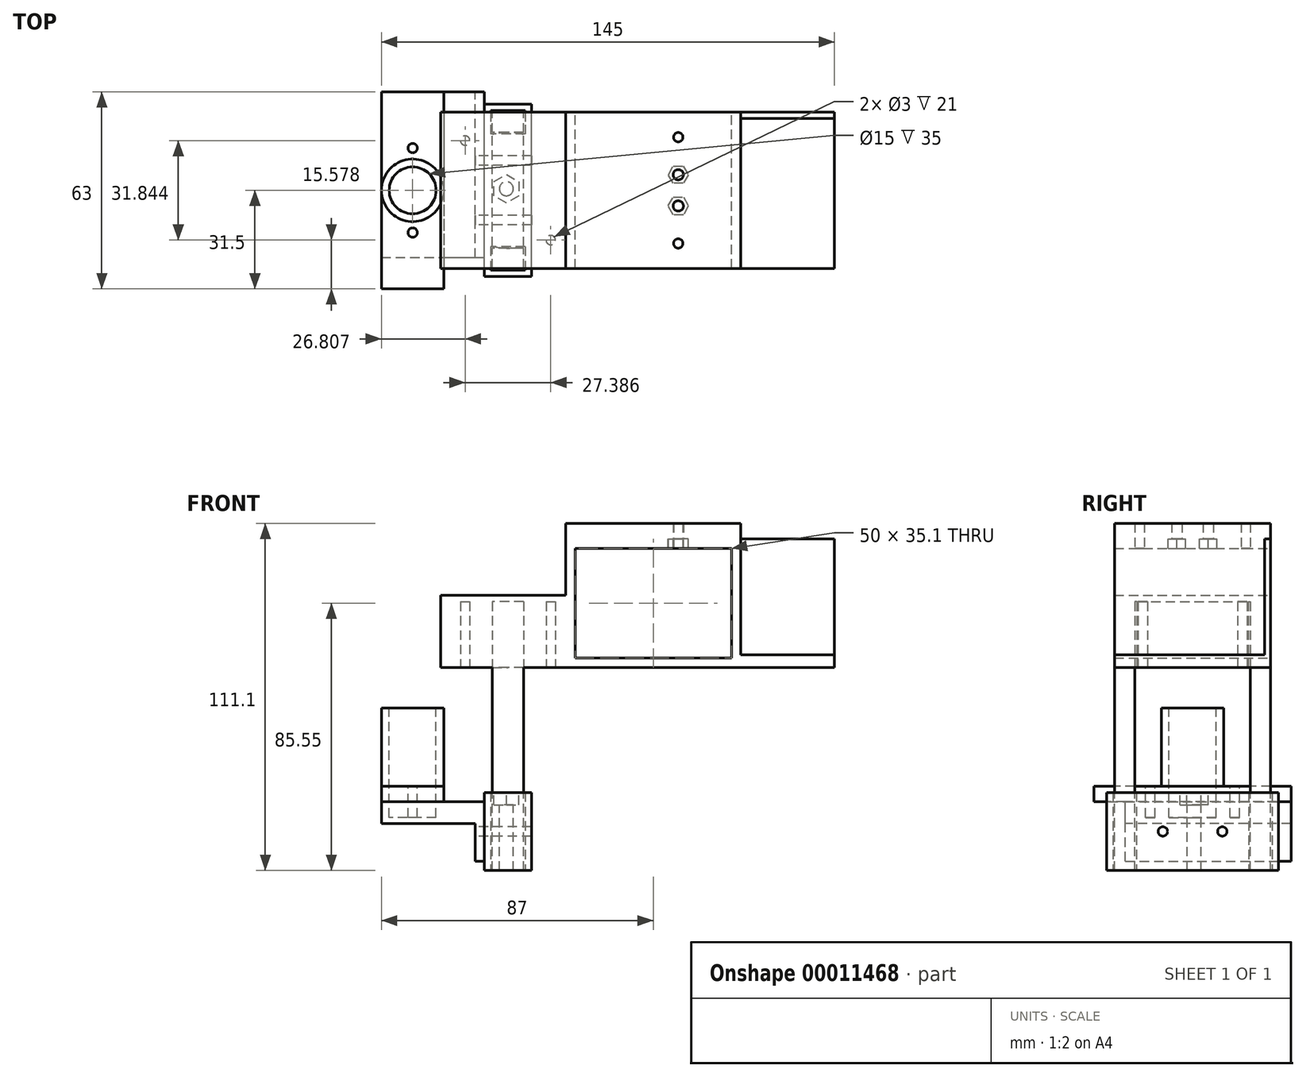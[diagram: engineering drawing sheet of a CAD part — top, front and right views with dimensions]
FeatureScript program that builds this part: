
annotation { "Feature Type Name" : "Feature", "Feature Type Description" : "" }
export const myFeature = defineFeature(function(context is Context, id is Id, definition is map)
    precondition{}
    {
        {
            var Q0;
            Q0=qCreatedBy(makeId("Front.planeOp"),FACE);
            var sketch = newSketch(context, id + "F0", { "sketchPlane" : qUnion([Q0])});
            skLineSegment(sketch, "E0.rect.bottom", {"start": v(-25, -17.55) * mm, "end": v(25, -17.55) * mm});
            skLineSegment(sketch, "E0.rect.top", {"start": v(-25, 17.55) * mm, "end": v(25, 17.55) * mm});
            skLineSegment(sketch, "E0.rect.left", {"start": v(-25, -17.55) * mm, "end": v(-25, 17.55) * mm});
            skLineSegment(sketch, "E0.rect.right", {"start": v(25, -17.55) * mm, "end": v(25, 17.55) * mm});
            skPoint(sketch, "E0.rect.middle", {"position": v(0, 0) * mm});
            skLineSegment(sketch, "E1.rect.bottom", {"start": v(-28, 20.55) * mm, "end": v(28, 20.55) * mm});
            skLineSegment(sketch, "E1.rect.top", {"start": v(-28, -20.55) * mm, "end": v(28, -20.55) * mm});
            skLineSegment(sketch, "E1.rect.left", {"start": v(-28, 20.55) * mm, "end": v(-28, -20.55) * mm});
            skLineSegment(sketch, "E1.rect.right", {"start": v(28, 20.55) * mm, "end": v(28, -20.55) * mm});
            skSolve(sketch);
        }
        {
            var Q0;
            Q0=makeQuery(id+"F0.imprint","IMPRINT",FACE,{"disambiguationData":[TD([[makeQuery(id+"F0.imprint","IMPRINT",EDGE,{"derivedFrom":sQuery(id+"F0.wireOp",EDGE,"E0.rect.bottom")}),-1.0]])]});
            extrude(context, id + "F1", {"entities" : qUnion([Q0]), "depth" : 50 * mm});
        }
        {
            var Q0;
            Q0=makeQuery(id+"F1.opExtrude","SWEPT_FACE",FACE,{"disambiguationData":[OSD([sQuery(id+"F0.wireOp",EDGE,"E1.rect.left")])]});
            extrude(context, id + "F2", {"entities" : qUnion([Q0]), "operationType" : NewBodyOperationType.ADD, "depth" : 40 * mm});
        }
        {
            var Q0;
            {var subQ0=sQuery(id+"F0.wireOp",EDGE,"E1.rect.top");Q0=makeQuery(id+"F2.boolean.opBoolean","MERGE",FACE,{"derivedFrom":[makeQuery(id+"F1.opExtrude","SWEPT_FACE",FACE,{"disambiguationData":[OSD([subQ0])]}),makeQuery(id+"F2.opExtrude","SWEPT_FACE",FACE,{"disambiguationData":[OSD([subQ0,sQuery(id+"F0.wireOp",EDGE,"E1.rect.left")])]})]});}
            var sketch = newSketch(context, id + "F3", { "sketchPlane" : qUnion([Q0])});
            skCircle(sketch, "E2", {"center": v(-46.5, 25) * mm, "radius": 18.5 * mm});
            skCircle(sketch, "E3", {"center": v(-60.2, 9.08) * mm, "radius": 1.5 * mm});
            skLineSegment(sketch, "E4", {"start": v(-68, 0) * mm, "end": v(-46.5, 25) * mm, "construction": true});
            skLineSegment(sketch, "E5", {"start": v(-46.5, 25) * mm, "end": v(-25, 50) * mm, "construction": true});
            skCircle(sketch, "E6", {"center": v(-32.8, 40.92) * mm, "radius": 1.5 * mm});
            skLineSegment(sketch, "E7.rect.bottom", {"start": v(-51.5, 50) * mm, "end": v(-41.5, 50) * mm});
            skLineSegment(sketch, "E7.rect.top", {"start": v(-51.5, 0) * mm, "end": v(-41.5, 0) * mm});
            skLineSegment(sketch, "E7.rect.left", {"start": v(-51.5, 50) * mm, "end": v(-51.5, 0) * mm});
            skLineSegment(sketch, "E7.rect.right", {"start": v(-41.5, 50) * mm, "end": v(-41.5, 0) * mm});
            skLineSegment(sketch, "E8.rect.bottom", {"start": v(-41.5, 6.5) * mm, "end": v(-51.5, 6.5) * mm});
            skLineSegment(sketch, "E8.rect.top", {"start": v(-41.5, 43.5) * mm, "end": v(-51.5, 43.5) * mm});
            skLineSegment(sketch, "E8.rect.left", {"start": v(-41.5, 6.5) * mm, "end": v(-41.5, 43.5) * mm});
            skLineSegment(sketch, "E8.rect.right", {"start": v(-51.5, 6.5) * mm, "end": v(-51.5, 43.5) * mm});
            skSolve(sketch);
        }
        {
            var Q0;
            {var subQ0=sQuery(id+"F3.wireOp",EDGE,"fb08d3f0-ee89-4665-98bc-1e5e658c65d8");var subQ1=sQuery(id+"F3.wireOp",EDGE,"E2");var subQ3=makeQuery(id+"F3.imprint","INTERSECT",VERTEX,{"disambiguationData":[OD(0.0)],"derivedFrom":[subQ1,subQ0]});Q0=makeQuery(id+"F3.imprint","IMPRINT",FACE,{"disambiguationData":[TD([[makeQuery(id+"F3.imprint","IMPRINT",EDGE,{"disambiguationData":[TD([[subQ3,1.0]])],"derivedFrom":subQ1}),1.0]])]});}
            var Q1;
            Q1=makeQuery(id+"F3.imprint","IMPRINT",FACE,{"disambiguationData":[TD([[makeQuery(id+"F3.imprint","IMPRINT",EDGE,{"derivedFrom":sQuery(id+"F3.wireOp",EDGE,"55c15fe1-b3bd-4285-8dcb-e304dae2f2c6")}),1.0]])]});
            var Q2;
            Q2=makeQuery(id+"F3.imprint","IMPRINT",FACE,{"disambiguationData":[TD([[makeQuery(id+"F3.imprint","IMPRINT",EDGE,{"derivedFrom":sQuery(id+"F3.wireOp",EDGE,"49e0d679-383e-4f4e-84bb-c1bf29e8086f")}),1.0]])]});
            var Q3;
            {var subQ0=sQuery(id+"F3.wireOp",EDGE,"fb08d3f0-ee89-4665-98bc-1e5e658c65d8");var subQ1=sQuery(id+"F3.wireOp",EDGE,"E2");var subQ3=makeQuery(id+"F3.imprint","INTERSECT",VERTEX,{"disambiguationData":[OD(0.0)],"derivedFrom":[subQ1,subQ0]});Q3=makeQuery(id+"F3.imprint","IMPRINT",FACE,{"disambiguationData":[TD([[makeQuery(id+"F3.imprint","IMPRINT",EDGE,{"disambiguationData":[TD([[subQ3,-1.0]])],"derivedFrom":subQ1}),1.0]])]});}
            var Q4;
            {var subQ1=sQuery(id+"F3.wireOp",EDGE,"E2");var subQ4=sQuery(id+"F3.wireOp",EDGE,"E7.rect.left");var subQ6=makeQuery(id+"F3.imprint","INTERSECT",VERTEX,{"disambiguationData":[OD(0.0)],"derivedFrom":[subQ1,subQ4]});Q4=makeQuery(id+"F3.imprint","IMPRINT",FACE,{"disambiguationData":[TD([[makeQuery(id+"F3.imprint","IMPRINT",EDGE,{"disambiguationData":[TD([[subQ6,1.0]])],"derivedFrom":subQ1}),1.0]])]});}
            var Q5;
            Q5=makeQuery(id+"F3.imprint","IMPRINT",FACE,{"disambiguationData":[TD([[makeQuery(id+"F3.imprint","IMPRINT",EDGE,{"derivedFrom":sQuery(id+"F3.wireOp",EDGE,"E3")}),1.0]])]});
            var Q6;
            Q6=makeQuery(id+"F3.imprint","IMPRINT",FACE,{"disambiguationData":[TD([[makeQuery(id+"F3.imprint","IMPRINT",EDGE,{"derivedFrom":sQuery(id+"F3.wireOp",EDGE,"E6")}),1.0]])]});
            var Q7;
            {var subQ1=sQuery(id+"F3.wireOp",EDGE,"E2");var subQ8=makeQuery(id+"F3.imprint","INTERSECT",VERTEX,{"derivedFrom":[subQ1,sQuery(id+"F3.wireOp",EDGE,"E8.rect.top")]});Q7=makeQuery(id+"F3.imprint","IMPRINT",FACE,{"disambiguationData":[TD([[makeQuery(id+"F3.imprint","IMPRINT",EDGE,{"disambiguationData":[TD([[subQ8,1.0]])],"derivedFrom":subQ1}),1.0]])]});}
            extrude(context, id + "F4", {"entities" : qUnion([Q0, Q1, Q2, Q3, Q4, Q5, Q6, Q7]), "operationType" : NewBodyOperationType.REMOVE, "oppositeDirection" : true, "depth" : 21 * mm});
        }
        {
            var Q0;
            {var subQ6=sQuery(id+"F3.wireOp",EDGE,"E7.rect.bottom");Q0=makeQuery(id+"F3.imprint","IMPRINT",FACE,{"disambiguationData":[TD([[makeQuery(id+"F3.imprint","IMPRINT",EDGE,{"derivedFrom":subQ6}),-1.0]])]});}
            var Q1;
            {var subQ6=sQuery(id+"F3.wireOp",EDGE,"E7.rect.top");Q1=makeQuery(id+"F3.imprint","IMPRINT",FACE,{"disambiguationData":[TD([[makeQuery(id+"F3.imprint","IMPRINT",EDGE,{"derivedFrom":subQ6}),1.0]])]});}
            extrude(context, id + "F5", {"entities" : qUnion([Q0, Q1]), "operationType" : NewBodyOperationType.ADD, "depth" : 65 * mm});
        }
        {
            var Q0;
            Q0=makeQuery(id+"F2.opExtrude","CAP_FACE",FACE,{"disambiguationData":[OSD([sQuery(id+"F0.wireOp",EDGE,"E1.rect.left")])],"isStart":false});
            var sketch = newSketch(context, id + "F6", { "sketchPlane" : qUnion([Q0])});
            skLineSegment(sketch, "E9", {"start": v(50, 2.45) * mm, "end": v(0, 2.45) * mm});
            skSolve(sketch);
        }
        {
            var Q0;
            {var subQ2=sQuery(id+"F6.wireOp",EDGE,"E9");Q0=makeQuery(id+"F6.imprint","IMPRINT",FACE,{"disambiguationData":[TD([[makeQuery(id+"F6.imprint","IMPRINT",EDGE,{"derivedFrom":subQ2}),-1.0]])]});}
            extrude(context, id + "F7", {"entities" : qUnion([Q0]), "operationType" : NewBodyOperationType.REMOVE, "oppositeDirection" : true, "depth" : 40 * mm});
        }
        {
            var Q0;
            Q0=makeQuery(id+"F1.opExtrude","SWEPT_FACE",FACE,{"disambiguationData":[OSD([sQuery(id+"F0.wireOp",EDGE,"E1.rect.right")])]});
            var sketch = newSketch(context, id + "F8", { "sketchPlane" : qUnion([Q0])});
            skLineSegment(sketch, "E10", {"start": v(-50, -16.55) * mm, "end": v(-2, -16.55) * mm});
            skLineSegment(sketch, "E11", {"start": v(-2, -16.55) * mm, "end": v(-2, 20.55) * mm});
            skSolve(sketch);
        }
        {
            var Q0;
            Q0 = qSketchRegion(id + "F8", true);
            var Q1;
            {var subQ2=sQuery(id+"F8.wireOp",EDGE,"E10");Q1=makeQuery(id+"F8.imprint","IMPRINT",FACE,{"disambiguationData":[TD([[makeQuery(id+"F8.imprint","IMPRINT",EDGE,{"derivedFrom":subQ2}),-1.0]])]});}
            extrude(context, id + "F9", {"entities" : qUnion([Q0, Q1]), "operationType" : NewBodyOperationType.ADD, "depth" : 30 * mm});
        }
        {
            var Q0;
            {var subQ0=sQuery(id+"F0.wireOp",EDGE,"E1.rect.bottom");Q0=makeQuery(id+"F9.boolean.opBoolean","MERGE",FACE,{"derivedFrom":[makeQuery(id+"F2.boolean.opBoolean","MERGE",FACE,{"derivedFrom":[makeQuery(id+"F1.opExtrude","SWEPT_FACE",FACE,{"disambiguationData":[OSD([subQ0])]}),makeQuery(id+"F2.opExtrude","SWEPT_FACE",FACE,{"disambiguationData":[OSD([subQ0,sQuery(id+"F0.wireOp",EDGE,"E1.rect.left")])]})]}),makeQuery(id+"F9.opExtrude","SWEPT_FACE",FACE,{"disambiguationData":[OSD([subQ0,sQuery(id+"F0.wireOp",EDGE,"E1.rect.right")])]})]});}
            var sketch = newSketch(context, id + "F10", { "sketchPlane" : qUnion([Q0])});
            skLineSegment(sketch, "E12", {"start": v(28, -2) * mm, "end": v(28, 0) * mm});
            skCircle(sketch, "E13", {"center": v(8, -20) * mm, "radius": 1.65 * mm});
            skCircle(sketch, "E14", {"center": v(8, -30) * mm, "radius": 1.65 * mm});
            skCircle(sketch, "E15.cCircle", {"center": v(8, -20) * mm, "radius": 2.75 * mm, "construction": true});
            skLineSegment(sketch, "E15.0", {"start": v(6.41, -17.25) * mm, "end": v(9.59, -17.25) * mm});
            skLineSegment(sketch, "E15.1", {"start": v(9.59, -17.25) * mm, "end": v(11.18, -20) * mm});
            skLineSegment(sketch, "E15.2", {"start": v(11.18, -20) * mm, "end": v(9.59, -22.75) * mm});
            skLineSegment(sketch, "E15.3", {"start": v(9.59, -22.75) * mm, "end": v(6.41, -22.75) * mm});
            skLineSegment(sketch, "E15.4", {"start": v(6.41, -22.75) * mm, "end": v(4.82, -20) * mm});
            skLineSegment(sketch, "E15.5", {"start": v(4.82, -20) * mm, "end": v(6.41, -17.25) * mm});
            skPoint(sketch, "E15.0.midPoint", {"position": v(8, -17.25) * mm});
            skCircle(sketch, "E16.cCircle", {"center": v(8, -30) * mm, "radius": 2.83 * mm, "construction": true});
            skLineSegment(sketch, "E16.0", {"start": v(6.37, -27.17) * mm, "end": v(9.63, -27.17) * mm});
            skLineSegment(sketch, "E16.1", {"start": v(9.63, -27.17) * mm, "end": v(11.27, -30) * mm});
            skLineSegment(sketch, "E16.2", {"start": v(11.27, -30) * mm, "end": v(9.63, -32.83) * mm});
            skLineSegment(sketch, "E16.3", {"start": v(9.63, -32.83) * mm, "end": v(6.37, -32.83) * mm});
            skLineSegment(sketch, "E16.4", {"start": v(6.37, -32.83) * mm, "end": v(4.73, -30) * mm});
            skLineSegment(sketch, "E16.5", {"start": v(4.73, -30) * mm, "end": v(6.37, -27.17) * mm});
            skPoint(sketch, "E16.0.midPoint", {"position": v(8, -27.17) * mm});
            skCircle(sketch, "E17", {"center": v(8, -42) * mm, "radius": 1.5 * mm});
            skCircle(sketch, "E18", {"center": v(8, -8) * mm, "radius": 1.5 * mm});
            skSolve(sketch);
        }
        {
            var Q0;
            Q0=makeQuery(id+"F10.imprint","IMPRINT",FACE,{"disambiguationData":[TD([[makeQuery(id+"F10.imprint","IMPRINT",EDGE,{"derivedFrom":sQuery(id+"F10.wireOp",EDGE,"E13")}),-1.0]])]});
            var Q1;
            Q1=makeQuery(id+"F10.imprint","IMPRINT",FACE,{"disambiguationData":[TD([[makeQuery(id+"F10.imprint","IMPRINT",EDGE,{"derivedFrom":sQuery(id+"F10.wireOp",EDGE,"E14")}),-1.0]])]});
            var Q2;
            {var subQ4=sQuery(id+"F10.wireOp",EDGE,"E12");Q2=makeQuery(id+"F10.imprint","IMPRINT",FACE,{"disambiguationData":[TD([[makeQuery(id+"F10.imprint","IMPRINT",EDGE,{"derivedFrom":subQ4}),1.0]])]});}
            extrude(context, id + "F11", {"entities" : qUnion([Q0, Q1, Q2]), "operationType" : NewBodyOperationType.ADD, "depth" : 5 * mm});
        }
        {
            var Q0;
            Q0=makeQuery(id+"F10.imprint","IMPRINT",FACE,{"disambiguationData":[TD([[makeQuery(id+"F10.imprint","IMPRINT",EDGE,{"derivedFrom":sQuery(id+"F10.wireOp",EDGE,"E18")}),1.0]])]});
            var Q1;
            Q1=makeQuery(id+"F10.imprint","IMPRINT",FACE,{"disambiguationData":[TD([[makeQuery(id+"F10.imprint","IMPRINT",EDGE,{"derivedFrom":sQuery(id+"F10.wireOp",EDGE,"E13")}),-1.0]])]});
            var Q2;
            Q2=makeQuery(id+"F10.imprint","IMPRINT",FACE,{"disambiguationData":[TD([[makeQuery(id+"F10.imprint","IMPRINT",EDGE,{"derivedFrom":sQuery(id+"F10.wireOp",EDGE,"E13")}),1.0]])]});
            var Q3;
            Q3=makeQuery(id+"F10.imprint","IMPRINT",FACE,{"disambiguationData":[TD([[makeQuery(id+"F10.imprint","IMPRINT",EDGE,{"derivedFrom":sQuery(id+"F10.wireOp",EDGE,"E14")}),-1.0]])]});
            var Q4;
            Q4=makeQuery(id+"F10.imprint","IMPRINT",FACE,{"disambiguationData":[TD([[makeQuery(id+"F10.imprint","IMPRINT",EDGE,{"derivedFrom":sQuery(id+"F10.wireOp",EDGE,"E14")}),1.0]])]});
            var Q5;
            Q5=makeQuery(id+"F10.imprint","IMPRINT",FACE,{"disambiguationData":[TD([[makeQuery(id+"F10.imprint","IMPRINT",EDGE,{"derivedFrom":sQuery(id+"F10.wireOp",EDGE,"E17")}),1.0]])]});
            extrude(context, id + "F12", {"entities" : qUnion([Q0, Q1, Q2, Q3, Q4, Q5]), "operationType" : NewBodyOperationType.REMOVE, "oppositeDirection" : true, "depth" : 3 * mm});
        }
        {
            var Q0;
            Q0=makeQuery(id+"F5.opExtrude","CAP_FACE",FACE,{"disambiguationData":[OSD([sQuery(id+"F3.wireOp",EDGE,"E7.rect.top"),sQuery(id+"F3.wireOp",EDGE,"E7.rect.left"),sQuery(id+"F3.wireOp",EDGE,"E7.rect.right"),sQuery(id+"F3.wireOp",EDGE,"E8.rect.bottom")])],"isStart":false});
            var sketch = newSketch(context, id + "F13", { "sketchPlane" : qUnion([Q0])});
            skLineSegment(sketch, "E19.bottom", {"start": v(-52, -0.5) * mm, "end": v(-41, -0.5) * mm});
            skLineSegment(sketch, "E19.top", {"start": v(-52, 50.5) * mm, "end": v(-41, 50.5) * mm});
            skLineSegment(sketch, "E19.left", {"start": v(-52, -0.5) * mm, "end": v(-52, 50.5) * mm});
            skLineSegment(sketch, "E19.right", {"start": v(-41, -0.5) * mm, "end": v(-41, 50.5) * mm});
            skLineSegment(sketch, "E20.bottom", {"start": v(-54, 52.5) * mm, "end": v(-39, 52.5) * mm});
            skLineSegment(sketch, "E20.top", {"start": v(-54, -2.5) * mm, "end": v(-39, -2.5) * mm});
            skLineSegment(sketch, "E20.left", {"start": v(-54, 52.5) * mm, "end": v(-54, -2.5) * mm});
            skLineSegment(sketch, "E20.right", {"start": v(-39, 52.5) * mm, "end": v(-39, -2.5) * mm});
            skLineSegment(sketch, "E21", {"start": v(-41, 43) * mm, "end": v(-52, 43) * mm});
            skLineSegment(sketch, "E22", {"start": v(-41, 41) * mm, "end": v(-52, 41) * mm});
            skLineSegment(sketch, "E23", {"start": v(-41, 7) * mm, "end": v(-52, 7) * mm});
            skLineSegment(sketch, "E24", {"start": v(-41, 9) * mm, "end": v(-52, 9) * mm});
            skLineSegment(sketch, "E25", {"start": v(-41, 41) * mm, "end": v(-39, 41) * mm});
            skLineSegment(sketch, "E26", {"start": v(-41, 9) * mm, "end": v(-39, 9) * mm});
            skLineSegment(sketch, "E27", {"start": v(-52, 9) * mm, "end": v(-54, 9) * mm});
            skLineSegment(sketch, "E28", {"start": v(-52, 41) * mm, "end": v(-54, 41) * mm});
            skSolve(sketch);
        }
        {
            var Q0;
            {var subQ9=sQuery(id+"F13.wireOp",EDGE,"E19.bottom");Q0=makeQuery(id+"F13.imprint","IMPRINT",FACE,{"disambiguationData":[TD([[makeQuery(id+"F13.imprint","IMPRINT",EDGE,{"derivedFrom":subQ9}),-1.0]])]});}
            var Q1;
            {var subQ1=sQuery(id+"F13.wireOp",EDGE,"E25");Q1=makeQuery(id+"F13.imprint","IMPRINT",FACE,{"disambiguationData":[TD([[makeQuery(id+"F13.imprint","IMPRINT",EDGE,{"derivedFrom":subQ1}),-1.0]])]});}
            var Q2;
            {var subQ7=sQuery(id+"F13.wireOp",EDGE,"E19.top");Q2=makeQuery(id+"F13.imprint","IMPRINT",FACE,{"disambiguationData":[TD([[makeQuery(id+"F13.imprint","IMPRINT",EDGE,{"derivedFrom":subQ7}),1.0]])]});}
            var Q3;
            {var subQ1=sQuery(id+"F13.wireOp",EDGE,"E27");Q3=makeQuery(id+"F13.imprint","IMPRINT",FACE,{"disambiguationData":[TD([[makeQuery(id+"F13.imprint","IMPRINT",EDGE,{"derivedFrom":subQ1}),-1.0]])]});}
            var Q4;
            {var subQ1=sQuery(id+"F13.wireOp",EDGE,"E21");Q4=makeQuery(id+"F13.imprint","IMPRINT",FACE,{"disambiguationData":[TD([[makeQuery(id+"F13.imprint","IMPRINT",EDGE,{"derivedFrom":subQ1}),1.0]])]});}
            var Q5;
            {var subQ1=sQuery(id+"F13.wireOp",EDGE,"E23");Q5=makeQuery(id+"F13.imprint","IMPRINT",FACE,{"disambiguationData":[TD([[makeQuery(id+"F13.imprint","IMPRINT",EDGE,{"derivedFrom":subQ1}),-1.0]])]});}
            var Q6;
            {var subQ1=sQuery(id+"F13.wireOp",EDGE,"E22");Q6=makeQuery(id+"F13.imprint","IMPRINT",FACE,{"disambiguationData":[TD([[makeQuery(id+"F13.imprint","IMPRINT",EDGE,{"derivedFrom":subQ1}),1.0]])]});}
            extrude(context, id + "F14", {"entities" : qUnion([Q0, Q1, Q2, Q3, Q4, Q5, Q6]), "oppositeDirection" : true, "depth" : 5 * mm});
        }
        {
            var Q0;
            Q0=makeQuery(id+"F14.opExtrude","CAP_FACE",FACE,{"disambiguationData":[OSD([sQuery(id+"F13.wireOp",EDGE,"E19.bottom"),sQuery(id+"F13.wireOp",EDGE,"E19.top"),sQuery(id+"F13.wireOp",EDGE,"E19.left"),sQuery(id+"F13.wireOp",EDGE,"E19.right"),sQuery(id+"F13.wireOp",EDGE,"E20.bottom"),sQuery(id+"F13.wireOp",EDGE,"E20.top"),sQuery(id+"F13.wireOp",EDGE,"E20.left"),sQuery(id+"F13.wireOp",EDGE,"E20.right"),sQuery(id+"F13.wireOp",EDGE,"E21"),sQuery(id+"F13.wireOp",EDGE,"E22"),sQuery(id+"F13.wireOp",EDGE,"E23"),sQuery(id+"F13.wireOp",EDGE,"E24")])],"isStart":false});
            var sketch = newSketch(context, id + "F15", { "sketchPlane" : qUnion([Q0])});
            skLineSegment(sketch, "E29", {"start": v(-39, 0.5) * mm, "end": v(-54, 0.5) * mm});
            skSolve(sketch);
        }
        {
            var Q0;
            {var subQ8=sQuery(id+"F13.wireOp",EDGE,"E19.bottom");Q0=makeQuery(id+"F15.imprint","IMPRINT",FACE,{"disambiguationData":[TD([[makeQuery(id+"F15.imprint","IMPRINT",EDGE,{"derivedFrom":makeQuery(id+"F14.opExtrude","CAP_EDGE",EDGE,{"disambiguationData":[OSD([subQ8])],"isStart":false})}),1.0]])]});}
            var Q1;
            {var subQ8=sQuery(id+"F13.wireOp",EDGE,"E19.top");Q1=makeQuery(id+"F15.imprint","IMPRINT",FACE,{"disambiguationData":[TD([[makeQuery(id+"F15.imprint","IMPRINT",EDGE,{"derivedFrom":makeQuery(id+"F14.opExtrude","CAP_EDGE",EDGE,{"disambiguationData":[OSD([subQ8])],"isStart":false})}),-1.0]])]});}
            var Q2;
            {var subQ3=makeQuery(id+"F14.opExtrude","CAP_EDGE",EDGE,{"disambiguationData":[OSD([sQuery(id+"F13.wireOp",EDGE,"E20.top")])],"isStart":false});Q2=makeQuery(id+"F15.imprint","IMPRINT",FACE,{"disambiguationData":[TD([[makeQuery(id+"F15.imprint","IMPRINT",EDGE,{"derivedFrom":subQ3}),-1.0]])]});}
            extrude(context, id + "F16", {"entities" : qUnion([Q0, Q1, Q2]), "operationType" : NewBodyOperationType.ADD, "depth" : 20 * mm});
        }
        {
            var Q0;
            Q0=makeQuery(id+"F16.opExtrude","CAP_FACE",FACE,{"disambiguationData":[OSD([sQuery(id+"F13.wireOp",EDGE,"E19.top"),sQuery(id+"F13.wireOp",EDGE,"E19.left"),sQuery(id+"F13.wireOp",EDGE,"E19.right"),sQuery(id+"F13.wireOp",EDGE,"E20.bottom"),sQuery(id+"F13.wireOp",EDGE,"E20.top"),sQuery(id+"F13.wireOp",EDGE,"E20.left"),sQuery(id+"F13.wireOp",EDGE,"E20.right"),sQuery(id+"F13.wireOp",EDGE,"E21"),sQuery(id+"F13.wireOp",EDGE,"E23"),sQuery(id+"F15.wireOp",EDGE,"E29")])],"isStart":false});
            var sketch = newSketch(context, id + "F17", { "sketchPlane" : qUnion([Q0])});
            skCircle(sketch, "E30", {"center": v(-47, -24.5) * mm, "radius": 2.25 * mm});
            skCircle(sketch, "E31.cCircle", {"center": v(-47, -24.5) * mm, "radius": 3.95 * mm, "construction": true});
            skLineSegment(sketch, "E31.0", {"start": v(-43.05, -22.22) * mm, "end": v(-43.05, -26.78) * mm});
            skLineSegment(sketch, "E31.1", {"start": v(-43.05, -26.78) * mm, "end": v(-47, -29.06) * mm});
            skLineSegment(sketch, "E31.2", {"start": v(-47, -29.06) * mm, "end": v(-50.95, -26.78) * mm});
            skLineSegment(sketch, "E31.3", {"start": v(-50.95, -26.78) * mm, "end": v(-50.95, -22.22) * mm});
            skLineSegment(sketch, "E31.4", {"start": v(-50.95, -22.22) * mm, "end": v(-47, -19.94) * mm});
            skLineSegment(sketch, "E31.5", {"start": v(-47, -19.94) * mm, "end": v(-43.05, -22.22) * mm});
            skPoint(sketch, "E31.0.midPoint", {"position": v(-43.05, -24.5) * mm});
            skSolve(sketch);
        }
        {
            var Q0;
            Q0=makeQuery(id+"F17.imprint","IMPRINT",FACE,{"disambiguationData":[TD([[makeQuery(id+"F17.imprint","IMPRINT",EDGE,{"derivedFrom":sQuery(id+"F17.wireOp",EDGE,"E30")}),1.0]])]});
            extrude(context, id + "F18", {"entities" : qUnion([Q0]), "operationType" : NewBodyOperationType.REMOVE, "oppositeDirection" : true, "depth" : 30 * mm});
        }
        {
            var Q0;
            Q0=makeQuery(id+"F17.imprint","IMPRINT",FACE,{"disambiguationData":[TD([[makeQuery(id+"F17.imprint","IMPRINT",EDGE,{"derivedFrom":sQuery(id+"F17.wireOp",EDGE,"E30")}),-1.0]])]});
            extrude(context, id + "F19", {"entities" : qUnion([Q0]), "operationType" : NewBodyOperationType.REMOVE, "oppositeDirection" : true, "depth" : 4 * mm});
        }
        {
            var Q0;
            {var subQ0=sQuery(id+"F13.wireOp",EDGE,"E20.left");Q0=makeQuery(id+"F16.boolean.opBoolean","MERGE",FACE,{"derivedFrom":[makeQuery(id+"FvFTa0KvEtPTojo_2.boolean.opBoolean","MERGE",FACE,{"derivedFrom":[makeQuery(id+"F14.opExtrude","SWEPT_FACE",FACE,{"disambiguationData":[OSD([subQ0])]}),makeQuery(id+"FvFTa0KvEtPTojo_2.opExtrude","SWEPT_FACE",FACE,{"disambiguationData":[OSD([subQ0]),TDD([makeQuery(id+"F13.imprint","IMPRINT",EDGE,{"disambiguationData":[TD([[makeQuery(id+"F13.imprint","INTERSECT",VERTEX,{"derivedFrom":[sQuery(id+"F13.wireOp",EDGE,"E20.bottom"),subQ0]}),-1.0]])],"derivedFrom":subQ0})])]}),makeQuery(id+"FvFTa0KvEtPTojo_2.opExtrude","SWEPT_FACE",FACE,{"disambiguationData":[OSD([subQ0]),TDD([makeQuery(id+"F13.imprint","IMPRINT",EDGE,{"disambiguationData":[TD([[makeQuery(id+"F13.imprint","INTERSECT",VERTEX,{"derivedFrom":[sQuery(id+"F13.wireOp",EDGE,"E20.top"),subQ0]}),1.0]])],"derivedFrom":subQ0})])]})]}),makeQuery(id+"F16.opExtrude","SWEPT_FACE",FACE,{"disambiguationData":[OSD([subQ0])]})]});}
            var sketch = newSketch(context, id + "F20", { "sketchPlane" : qUnion([Q0])});
            skPoint(sketch, "E32", {"position": v(15.5, -73.05) * mm});
            skPoint(sketch, "E33", {"position": v(34.5, -73.05) * mm});
            skLineSegment(sketch, "E34.rect.bottom", {"start": v(46.5, -82.55) * mm, "end": v(3.5, -82.55) * mm});
            skLineSegment(sketch, "E34.rect.top", {"start": v(46.5, -63.55) * mm, "end": v(3.5, -63.55) * mm});
            skLineSegment(sketch, "E34.rect.left", {"start": v(46.5, -82.55) * mm, "end": v(46.5, -63.55) * mm});
            skLineSegment(sketch, "E34.rect.right", {"start": v(3.5, -82.55) * mm, "end": v(3.5, -63.55) * mm});
            skPoint(sketch, "E34.rect.middle", {"position": v(25, -73.05) * mm});
            skSolve(sketch);
        }
        {
            var Q0;
            Q0=sQuery(id+"F20.wireOp",VERTEX,"E32");
            var Q1;
            Q1=sQuery(id+"F20.wireOp",VERTEX,"E33");
            var Q2;
            Q2=makeQuery(id+"F14.opExtrude","SWEPT_BODY",BODY,{"disambiguationData":[OSD([sQuery(id+"F13.wireOp",EDGE,"E19.bottom"),sQuery(id+"F13.wireOp",EDGE,"E19.top"),sQuery(id+"F13.wireOp",EDGE,"E19.left"),sQuery(id+"F13.wireOp",EDGE,"E19.right"),sQuery(id+"F13.wireOp",EDGE,"E20.bottom"),sQuery(id+"F13.wireOp",EDGE,"E20.top"),sQuery(id+"F13.wireOp",EDGE,"E20.left"),sQuery(id+"F13.wireOp",EDGE,"E20.right"),sQuery(id+"F13.wireOp",EDGE,"E21"),sQuery(id+"F13.wireOp",EDGE,"E23")])]});
            hole(context, id + "F21", {"style" : HoleStyle.SIMPLE, "holeDiameter" : 3 * mm, "endStyle" : HoleEndStyle.THROUGH, "locations" : qUnion([Q0, Q1]), "scope" : qUnion([Q2])});
        }
        {
            var Q0;
            Q0 = qSketchRegion(id + "F20", true);
            extrude(context, id + "F22", {"entities" : qUnion([Q0]), "depth" : 3 * mm});
        }
        {
            var Q0;
            Q0=makeQuery(id+"F22.opExtrude","CAP_FACE",FACE,{"disambiguationData":[OSD([sQuery(id+"F20.wireOp",EDGE,"E34.rect.bottom"),sQuery(id+"F20.wireOp",EDGE,"E34.rect.top"),sQuery(id+"F20.wireOp",EDGE,"E34.rect.left"),sQuery(id+"F20.wireOp",EDGE,"E34.rect.right")])],"isStart":false});
            var sketch = newSketch(context, id + "F23", { "sketchPlane" : qUnion([Q0])});
            skLineSegment(sketch, "E35.top", {"start": v(3.5, -70.55) * mm, "end": v(46.5, -70.55) * mm});
            skLineSegment(sketch, "E35.left", {"start": v(3.5, -67.55) * mm, "end": v(3.5, -70.55) * mm});
            skLineSegment(sketch, "E35.right", {"start": v(46.5, -67.55) * mm, "end": v(46.5, -70.55) * mm});
            skSolve(sketch);
        }
        {
            var Q0;
            Q0=makeQuery(id+"F23.imprint","IMPRINT",FACE,{"disambiguationData":[TD([[makeQuery(id+"F23.imprint","IMPRINT",EDGE,{"derivedFrom":sQuery(id+"F23.wireOp",EDGE,"E35.top")}),1.0]])]});
            extrude(context, id + "F24", {"entities" : qUnion([Q0]), "operationType" : NewBodyOperationType.ADD, "depth" : 30 * mm});
        }
        {
            var Q0;
            Q0=sQuery(id+"F20.wireOp",VERTEX,"E33");
            var Q1;
            Q1=sQuery(id+"F20.wireOp",VERTEX,"E32");
            var Q2;
            Q2=makeQuery(id+"F22.opExtrude","SWEPT_BODY",BODY,{"disambiguationData":[OSD([sQuery(id+"F20.wireOp",EDGE,"E34.rect.bottom"),sQuery(id+"F20.wireOp",EDGE,"E34.rect.top"),sQuery(id+"F20.wireOp",EDGE,"E34.rect.left"),sQuery(id+"F20.wireOp",EDGE,"E34.rect.right")])]});
            hole(context, id + "F25", {"style" : HoleStyle.SIMPLE, "holeDiameter" : 3 * mm, "endStyle" : HoleEndStyle.THROUGH, "oppositeDirection" : true, "locations" : qUnion([Q0, Q1]), "scope" : qUnion([Q2])});
        }
        {
            var Q0;
            {var subQ0=sQuery(id+"F20.wireOp",EDGE,"E34.rect.top");Q0=makeQuery(id+"F24.boolean.opBoolean","MERGE",FACE,{"derivedFrom":[makeQuery(id+"F22.opExtrude","SWEPT_FACE",FACE,{"disambiguationData":[OSD([subQ0])]}),makeQuery(id+"F24.opExtrude","SWEPT_FACE",FACE,{"disambiguationData":[OSD([subQ0])]})]});}
            var sketch = newSketch(context, id + "F26", { "sketchPlane" : qUnion([Q0])});
            skCircle(sketch, "E36", {"center": v(-77, -25) * mm, "radius": 7.5 * mm});
            skCircle(sketch, "E37", {"center": v(-77, -11.5) * mm, "radius": 1.5 * mm});
            skCircle(sketch, "E38", {"center": v(-77, -38.5) * mm, "radius": 1.5 * mm});
            skLineSegment(sketch, "E39", {"start": v(-67, -3.5) * mm, "end": v(-67, -46.5) * mm});
            skSolve(sketch);
        }
        {
            var Q0;
            Q0=makeQuery(id+"F26.imprint","IMPRINT",FACE,{"disambiguationData":[TD([[makeQuery(id+"F26.imprint","IMPRINT",EDGE,{"derivedFrom":sQuery(id+"F26.wireOp",EDGE,"E36")}),1.0]])]});
            var Q1;
            Q1=makeQuery(id+"F26.imprint","IMPRINT",FACE,{"disambiguationData":[TD([[makeQuery(id+"F26.imprint","IMPRINT",EDGE,{"derivedFrom":sQuery(id+"F26.wireOp",EDGE,"E38")}),1.0]])]});
            var Q2;
            Q2=makeQuery(id+"F26.imprint","IMPRINT",FACE,{"disambiguationData":[TD([[makeQuery(id+"F26.imprint","IMPRINT",EDGE,{"derivedFrom":sQuery(id+"F26.wireOp",EDGE,"E37")}),1.0]])]});
            extrude(context, id + "F27", {"entities" : qUnion([Q0, Q1, Q2]), "operationType" : NewBodyOperationType.REMOVE, "oppositeDirection" : true, "depth" : 5 * mm});
        }
        {
            var Q0;
            Q0=makeQuery(id+"F26.imprint","IMPRINT",FACE,{"disambiguationData":[TD([[makeQuery(id+"F26.imprint","IMPRINT",EDGE,{"derivedFrom":sQuery(id+"F26.wireOp",EDGE,"E36")}),-1.0]])]});
            extrude(context, id + "F28", {"entities" : qUnion([Q0]), "depth" : 5 * mm});
        }
        {
            var Q0;
            Q0=makeQuery(id+"F28.opExtrude","CAP_FACE",FACE,{"disambiguationData":[OSD([sQuery(id+"F20.wireOp",EDGE,"E34.rect.top"),sQuery(id+"F20.wireOp",EDGE,"E34.rect.left"),sQuery(id+"F20.wireOp",EDGE,"E34.rect.right"),sQuery(id+"F26.wireOp",EDGE,"E36"),sQuery(id+"F26.wireOp",EDGE,"E37"),sQuery(id+"F26.wireOp",EDGE,"E38"),sQuery(id+"F26.wireOp",EDGE,"E39")])],"isStart":false});
            var sketch = newSketch(context, id + "F29", { "sketchPlane" : qUnion([Q0])});
            skCircle(sketch, "E40", {"center": v(-77, -25) * mm, "radius": 10 * mm});
            skSolve(sketch);
        }
        {
            var Q0;
            Q0=makeQuery(id+"F29.imprint","IMPRINT",FACE,{"disambiguationData":[TD([[makeQuery(id+"F29.imprint","IMPRINT",EDGE,{"derivedFrom":makeQuery(id+"F28.opExtrude","CAP_EDGE",EDGE,{"disambiguationData":[OSD([sQuery(id+"F26.wireOp",EDGE,"E36")])],"isStart":false})}),-1.0]])]});
            extrude(context, id + "F30", {"entities" : qUnion([Q0]), "operationType" : NewBodyOperationType.ADD, "depth" : 25 * mm});
        }
        {
            var Q0;
            Q0=makeQuery(id+"F28.opExtrude","SWEPT_FACE",FACE,{"disambiguationData":[OSD([sQuery(id+"F20.wireOp",EDGE,"E34.rect.top"),sQuery(id+"F20.wireOp",EDGE,"E34.rect.left")])]});
            extrude(context, id + "F31", {"entities" : qUnion([Q0]), "operationType" : NewBodyOperationType.ADD, "depth" : 10 * mm});
        }
        {
            var Q0;
            Q0=makeQuery(id+"F28.opExtrude","SWEPT_FACE",FACE,{"disambiguationData":[OSD([sQuery(id+"F20.wireOp",EDGE,"E34.rect.top"),sQuery(id+"F20.wireOp",EDGE,"E34.rect.right")])]});
            extrude(context, id + "F32", {"entities" : qUnion([Q0]), "operationType" : NewBodyOperationType.ADD, "depth" : 10 * mm});
        }
    });
